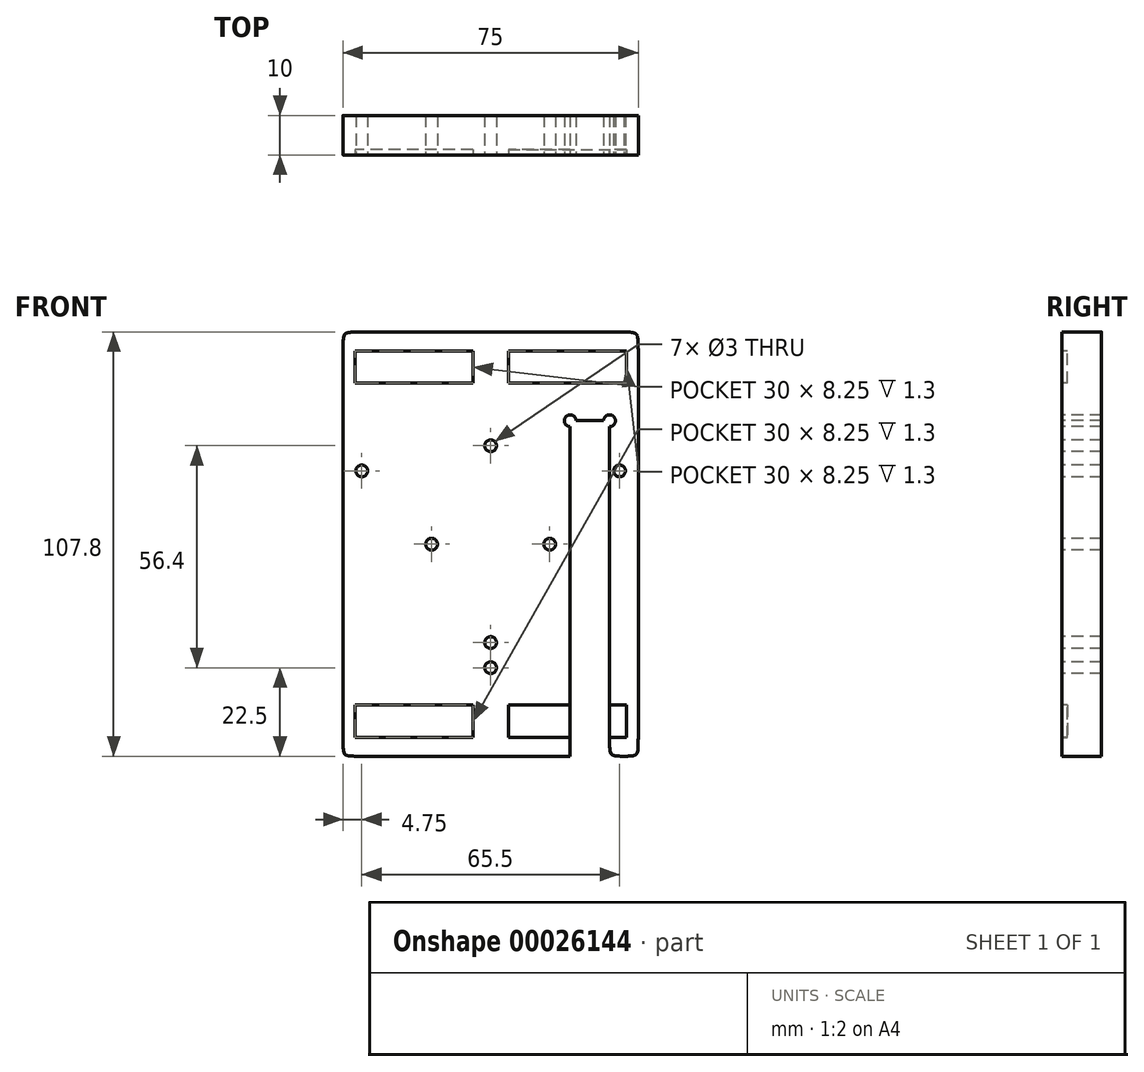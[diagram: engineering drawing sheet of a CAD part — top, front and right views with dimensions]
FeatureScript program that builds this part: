
annotation { "Feature Type Name" : "Feature", "Feature Type Description" : "" }
export const myFeature = defineFeature(function(context is Context, id is Id, definition is map)
    precondition{}
    {
        {
            var Q0;
            Q0=qCreatedBy(makeId("Front.planeOp"),FACE);
            var sketch = newSketch(context, id + "F0", { "sketchPlane" : qUnion([Q0])});
            skLineSegment(sketch, "E0.rect.bottom", {"start": v(37.5, -53.9) * mm, "end": v(30.2, -53.9) * mm});
            skLineSegment(sketch, "E0.rect.top", {"start": v(37.5, 53.9) * mm, "end": v(-37.5, 53.9) * mm});
            skLineSegment(sketch, "E0.rect.left", {"start": v(37.5, -53.9) * mm, "end": v(37.5, 53.9) * mm});
            skLineSegment(sketch, "E0.rect.right", {"start": v(-37.5, -53.9) * mm, "end": v(-37.5, 53.9) * mm});
            skPoint(sketch, "E0.rect.middle", {"position": v(0, 0) * mm});
            skLineSegment(sketch, "E1", {"start": v(-37.5, 45) * mm, "end": v(37.5, 45) * mm, "construction": true});
            skLineSegment(sketch, "E2", {"start": v(37.5, 45) * mm, "end": v(-37.5, -45) * mm, "construction": true});
            skLineSegment(sketch, "E3", {"start": v(-37.5, -45) * mm, "end": v(37.5, -45) * mm, "construction": true});
            skLineSegment(sketch, "E4.rect.bottom", {"start": v(-4.5, 40.87) * mm, "end": v(-34.5, 40.87) * mm});
            skLineSegment(sketch, "E4.rect.top", {"start": v(-4.5, 49.12) * mm, "end": v(-34.5, 49.12) * mm});
            skLineSegment(sketch, "E4.rect.left", {"start": v(-4.5, 40.87) * mm, "end": v(-4.5, 49.12) * mm});
            skLineSegment(sketch, "E4.rect.right", {"start": v(-34.5, 40.87) * mm, "end": v(-34.5, 49.12) * mm});
            skPoint(sketch, "E4.rect.middle", {"position": v(-19.5, 45) * mm});
            skLineSegment(sketch, "E5.rect.bottom", {"start": v(4.5, 40.87) * mm, "end": v(34.5, 40.87) * mm});
            skLineSegment(sketch, "E5.rect.top", {"start": v(4.5, 49.12) * mm, "end": v(34.5, 49.12) * mm});
            skLineSegment(sketch, "E5.rect.left", {"start": v(4.5, 40.87) * mm, "end": v(4.5, 49.12) * mm});
            skLineSegment(sketch, "E5.rect.right", {"start": v(34.5, 40.87) * mm, "end": v(34.5, 49.12) * mm});
            skPoint(sketch, "E5.rect.middle", {"position": v(19.5, 45) * mm});
            skLineSegment(sketch, "E6.rect.bottom", {"start": v(-4.5, -49.12) * mm, "end": v(-34.5, -49.12) * mm});
            skLineSegment(sketch, "E6.rect.top", {"start": v(-4.5, -40.88) * mm, "end": v(-34.5, -40.88) * mm});
            skLineSegment(sketch, "E6.rect.left", {"start": v(-4.5, -49.12) * mm, "end": v(-4.5, -40.88) * mm});
            skLineSegment(sketch, "E6.rect.right", {"start": v(-34.5, -49.12) * mm, "end": v(-34.5, -40.88) * mm});
            skPoint(sketch, "E6.rect.middle", {"position": v(-19.5, -45) * mm});
            skLineSegment(sketch, "E7.rect.bottom", {"start": v(34.5, -49.12) * mm, "end": v(30.2, -49.12) * mm});
            skLineSegment(sketch, "E7.rect.top", {"start": v(34.5, -40.87) * mm, "end": v(30.2, -40.87) * mm});
            skLineSegment(sketch, "E7.rect.left", {"start": v(34.5, -49.12) * mm, "end": v(34.5, -40.87) * mm});
            skLineSegment(sketch, "E7.rect.right", {"start": v(4.5, -49.12) * mm, "end": v(4.5, -40.87) * mm});
            skPoint(sketch, "E7.rect.middle", {"position": v(19.5, -45) * mm});
            skLineSegment(sketch, "E8", {"start": v(0, -25) * mm, "end": v(0, 25) * mm, "construction": true});
            skLineSegment(sketch, "E9", {"start": v(-15, 0) * mm, "end": v(15, 0) * mm, "construction": true});
            skCircle(sketch, "E10", {"center": v(0, 25) * mm, "radius": 1.5 * mm});
            skCircle(sketch, "E11", {"center": v(15, 0) * mm, "radius": 1.5 * mm});
            skCircle(sketch, "E12", {"center": v(0, -25) * mm, "radius": 1.5 * mm});
            skCircle(sketch, "E13", {"center": v(-15, 0) * mm, "radius": 1.5 * mm});
            skPoint(sketch, "E14.rect.middle", {"position": v(25.15, 0) * mm});
            skPoint(sketch, "E15.orphan", {"position": v(20.1, 30.28) * mm});
            skPoint(sketch, "E14.rect.right.end.orphan", {"position": v(30.2, 30.91) * mm});
            skPoint(sketch, "E14.rect.bottom.end.orphan", {"position": v(30.2, -30.28) * mm});
            skPoint(sketch, "E14.rect.bottom.start.orphan", {"position": v(20.1, -30.91) * mm});
            skLineSegment(sketch, "E16.rect.top", {"start": v(28.7, 31.37) * mm, "end": v(21.7, 31.37) * mm});
            skLineSegment(sketch, "E16.rect.left", {"start": v(30.2, -53.9) * mm, "end": v(30.2, 29.87) * mm});
            skPoint(sketch, "E16.rect.middle", {"position": v(25.2, 0.31) * mm});
            skArc(sketch, "E17", {"start": v(21.7, 31.37) * mm, "mid": v(19.14, 32.43) * mm, "end": v(20.2, 29.87) * mm});
            skArc(sketch, "E18", {"start": v(30.2, 29.87) * mm, "mid": v(31.26, 32.43) * mm, "end": v(28.7, 31.37) * mm});
            skLineSegment(sketch, "E19.trimOffspring", {"start": v(20.2, -53.9) * mm, "end": v(20.2, 29.87) * mm});
            skPoint(sketch, "E20.center.orphan", {"position": v(20.2, -30.74) * mm});
            skPoint(sketch, "E21.center.orphan", {"position": v(30.2, -30.74) * mm});
            skLineSegment(sketch, "E22.trimOffspring", {"start": v(20.2, -40.87) * mm, "end": v(4.5, -40.87) * mm});
            skLineSegment(sketch, "E23.trimOffspring", {"start": v(20.2, -49.12) * mm, "end": v(4.5, -49.12) * mm});
            skLineSegment(sketch, "E24.trimOffspring", {"start": v(20.2, -53.9) * mm, "end": v(-37.5, -53.9) * mm});
            skLineSegment(sketch, "E25", {"start": v(-37.5, 18.6) * mm, "end": v(37.5, 18.6) * mm, "construction": true});
            skCircle(sketch, "E26", {"center": v(-32.75, 18.6) * mm, "radius": 1.5 * mm});
            skCircle(sketch, "E27.MirrorC", {"center": v(32.75, 18.6) * mm, "radius": 1.5 * mm});
            skCircle(sketch, "E28", {"center": v(0, -31.4) * mm, "radius": 1.5 * mm});
            skSolve(sketch);
        }
        {
            var Q0;
            Q0=makeQuery(id+"F0.imprint","IMPRINT",FACE,{"disambiguationData":[TD([[makeQuery(id+"F0.imprint","IMPRINT",EDGE,{"derivedFrom":sQuery(id+"F0.wireOp",EDGE,"E0.rect.bottom")}),-1.0]])]});
            var Q1;
            Q1=makeQuery(id+"F0.imprint","IMPRINT",FACE,{"disambiguationData":[TD([[makeQuery(id+"F0.imprint","IMPRINT",EDGE,{"derivedFrom":sQuery(id+"F0.wireOp",EDGE,"E4.rect.bottom")}),-1.0]])]});
            var Q2;
            Q2=makeQuery(id+"F0.imprint","IMPRINT",FACE,{"disambiguationData":[TD([[makeQuery(id+"F0.imprint","IMPRINT",EDGE,{"derivedFrom":sQuery(id+"F0.wireOp",EDGE,"E5.rect.bottom")}),1.0]])]});
            var Q3;
            Q3=makeQuery(id+"F0.imprint","IMPRINT",FACE,{"disambiguationData":[TD([[makeQuery(id+"F0.imprint","IMPRINT",EDGE,{"derivedFrom":sQuery(id+"F0.wireOp",EDGE,"E6.rect.bottom")}),-1.0]])]});
            var Q4;
            Q4=makeQuery(id+"F0.imprint","IMPRINT",FACE,{"disambiguationData":[TD([[makeQuery(id+"F0.imprint","IMPRINT",EDGE,{"derivedFrom":sQuery(id+"F0.wireOp",EDGE,"E7.rect.bottom")}),-1.0]])]});
            var Q5;
            Q5=makeQuery(id+"F0.imprint","IMPRINT",FACE,{"disambiguationData":[TD([[makeQuery(id+"F0.imprint","IMPRINT",EDGE,{"derivedFrom":sQuery(id+"F0.wireOp",EDGE,"E7.rect.right")}),-1.0]])]});
            extrude(context, id + "F1", {"entities" : qUnion([Q0, Q1, Q2, Q3, Q4, Q5]), "oppositeDirection" : true, "depth" : 10 * mm});
        }
        {
            var Q0;
            Q0=makeQuery(id+"F1.opExtrude","SWEPT_EDGE",EDGE,{"disambiguationData":[OSD([sQuery(id+"F0.wireOp",EDGE,"E0.rect.top"),sQuery(id+"F0.wireOp",EDGE,"E0.rect.right")])]});
            var Q1;
            Q1=makeQuery(id+"F1.opExtrude","SWEPT_EDGE",EDGE,{"disambiguationData":[OSD([sQuery(id+"F0.wireOp",EDGE,"E0.rect.bottom"),sQuery(id+"F0.wireOp",EDGE,"E0.rect.right")])]});
            var Q2;
            Q2=makeQuery(id+"F1.opExtrude","SWEPT_EDGE",EDGE,{"disambiguationData":[OSD([sQuery(id+"F0.wireOp",EDGE,"E0.rect.bottom"),sQuery(id+"F0.wireOp",EDGE,"E0.rect.left")])]});
            var Q3;
            Q3=makeQuery(id+"F1.opExtrude","SWEPT_EDGE",EDGE,{"disambiguationData":[OSD([sQuery(id+"F0.wireOp",EDGE,"E0.rect.top"),sQuery(id+"F0.wireOp",EDGE,"E0.rect.left")])]});
            fillet(context, id + "F2", {"entities" : qUnion([Q0, Q1, Q2, Q3]), "radius" : 5 * mm, "tangentPropagation" : true, "rho" : 0.8, "crossSection" : FilletCrossSection.CONIC, "allowEdgeOverflow" : false});
        }
        {
            var Q0;
            Q0=makeQuery(id+"F0.imprint","IMPRINT",FACE,{"disambiguationData":[TD([[makeQuery(id+"F0.imprint","IMPRINT",EDGE,{"derivedFrom":sQuery(id+"F0.wireOp",EDGE,"E4.rect.bottom")}),-1.0]])]});
            var Q1;
            Q1=makeQuery(id+"F0.imprint","IMPRINT",FACE,{"disambiguationData":[TD([[makeQuery(id+"F0.imprint","IMPRINT",EDGE,{"derivedFrom":sQuery(id+"F0.wireOp",EDGE,"E5.rect.bottom")}),1.0]])]});
            var Q2;
            Q2=makeQuery(id+"F0.imprint","IMPRINT",FACE,{"disambiguationData":[TD([[makeQuery(id+"F0.imprint","IMPRINT",EDGE,{"derivedFrom":sQuery(id+"F0.wireOp",EDGE,"E6.rect.bottom")}),-1.0]])]});
            var Q3;
            Q3=makeQuery(id+"F0.imprint","IMPRINT",FACE,{"disambiguationData":[TD([[makeQuery(id+"F0.imprint","IMPRINT",EDGE,{"derivedFrom":sQuery(id+"F0.wireOp",EDGE,"E7.rect.right")}),-1.0]])]});
            var Q4;
            {var subQ2=sQuery(id+"F0.wireOp",EDGE,"E7.rect.bottom");Q4=makeQuery(id+"F0.imprint","IMPRINT",FACE,{"disambiguationData":[TD([[makeQuery(id+"F0.imprint","IMPRINT",EDGE,{"derivedFrom":subQ2}),-1.0]])]});}
            extrude(context, id + "F3", {"entities" : qUnion([Q0, Q1, Q2, Q3, Q4]), "operationType" : NewBodyOperationType.REMOVE, "oppositeDirection" : true, "depth" : 1.3 * mm});
        }
    });
